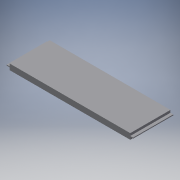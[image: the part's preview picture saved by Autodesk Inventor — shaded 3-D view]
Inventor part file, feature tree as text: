
AUTODESK INVENTOR PART (.ipt)
format: ipt  version: 2018 (Build 220112000, 112)  size: 104,448 bytes
history: native  units: mm
features: extrude x3, sketch x3
ambient origin geometry x8: Origin, YZ Plane, XZ Plane, XY Plane, X Axis, Y Axis, Z Axis, Center Point
bodies: Solid1 (feature_tree)
feature tree (6):
  extrude  "Extrusion1"  Depth=14.0mm
  extrude  "Extrusion2"  Depth=0.85mm
  extrude  "Extrusion3"  Depth=1.0mm TaperAngle=0.0deg
  sketch  "Sketch1"  dims[d0=42.0mm d1=14.0mm]
  sketch  "Sketch2"  dims[d2=2.0mm d3=0.0mm d4=0.85mm]
  sketch  "Sketch3"  dims[d5=0.3mm d6=1.0mm d7=0.0mm d8=1.0mm d9=0.0mm]
